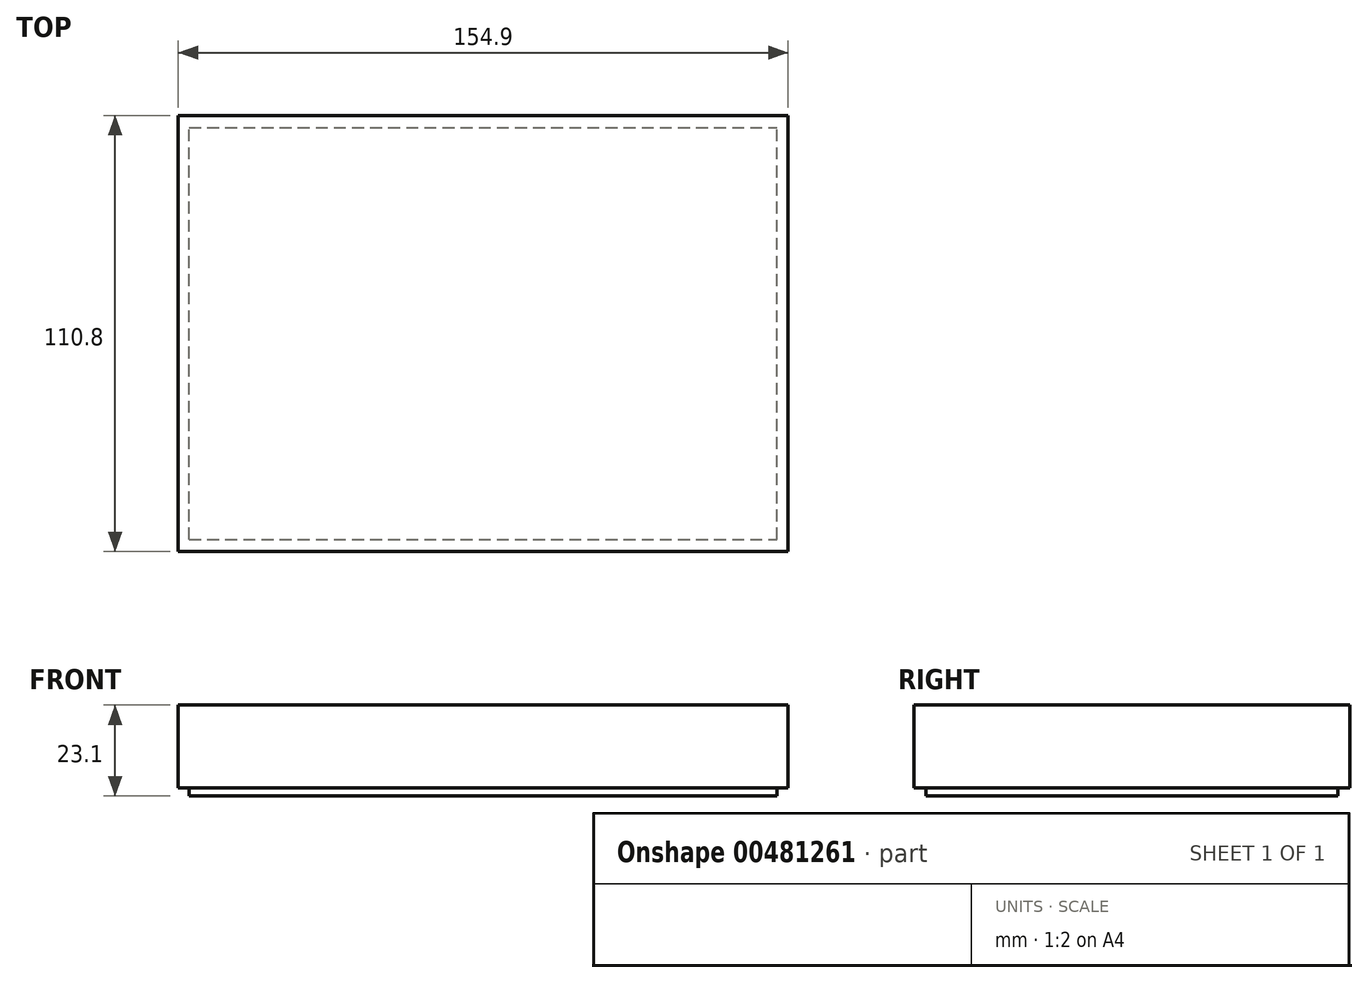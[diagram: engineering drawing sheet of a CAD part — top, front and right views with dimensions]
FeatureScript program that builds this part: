
annotation { "Feature Type Name" : "Feature", "Feature Type Description" : "" }
export const myFeature = defineFeature(function(context is Context, id is Id, definition is map)
    precondition{}
    {
        {
            var Q0;
            Q0=qCreatedBy(makeId("Front.planeOp"),FACE);
            var sketch = newSketch(context, id + "F0", { "sketchPlane" : qUnion([Q0])});
            skLineSegment(sketch, "E0.bottom", {"start": v(-77.45, 10.55) * mm, "end": v(77.45, 10.55) * mm});
            skLineSegment(sketch, "E0.top", {"start": v(-77.45, -10.55) * mm, "end": v(77.45, -10.55) * mm});
            skLineSegment(sketch, "E0.left", {"start": v(-77.45, 10.55) * mm, "end": v(-77.45, -10.55) * mm});
            skLineSegment(sketch, "E0.right", {"start": v(77.45, 10.55) * mm, "end": v(77.45, -10.55) * mm});
            skPoint(sketch, "E0.middle", {"position": v(0, 0) * mm});
            skLineSegment(sketch, "E1.bottom", {"start": v(-74.68, -12.55) * mm, "end": v(74.68, -12.55) * mm});
            skLineSegment(sketch, "E1.top", {"start": v(-74.68, -8.55) * mm, "end": v(74.68, -8.55) * mm});
            skLineSegment(sketch, "E1.left", {"start": v(-74.68, -12.55) * mm, "end": v(-74.68, -8.55) * mm});
            skLineSegment(sketch, "E1.right", {"start": v(74.68, -12.55) * mm, "end": v(74.68, -8.55) * mm});
            skPoint(sketch, "E1.middle", {"position": v(0, -10.55) * mm});
            skSolve(sketch);
        }
        {
            var Q0;
            {var subQ5=sQuery(id+"F0.wireOp",EDGE,"E1.top");Q0=makeQuery(id+"F0.imprint","IMPRINT",FACE,{"disambiguationData":[TD([[makeQuery(id+"F0.imprint","IMPRINT",EDGE,{"derivedFrom":subQ5}),-1.0]])]});}
            var Q1;
            Q1=makeQuery(id+"F0.imprint","IMPRINT",FACE,{"disambiguationData":[TD([[makeQuery(id+"F0.imprint","IMPRINT",EDGE,{"derivedFrom":sQuery(id+"F0.wireOp",EDGE,"E0.bottom")}),-1.0]])]});
            extrude(context, id + "F1", {"entities" : qUnion([Q0, Q1]), "endBound" : BoundingType.SYMMETRIC, "depth" : 110.8 * mm});
        }
        {
            var Q0;
            {var subQ5=sQuery(id+"F0.wireOp",EDGE,"E1.bottom");Q0=makeQuery(id+"F0.imprint","IMPRINT",FACE,{"disambiguationData":[TD([[makeQuery(id+"F0.imprint","IMPRINT",EDGE,{"derivedFrom":subQ5}),1.0]])]});}
            extrude(context, id + "F2", {"entities" : qUnion([Q0]), "operationType" : NewBodyOperationType.ADD, "endBound" : BoundingType.SYMMETRIC, "depth" : 104.64 * mm});
        }
    });
